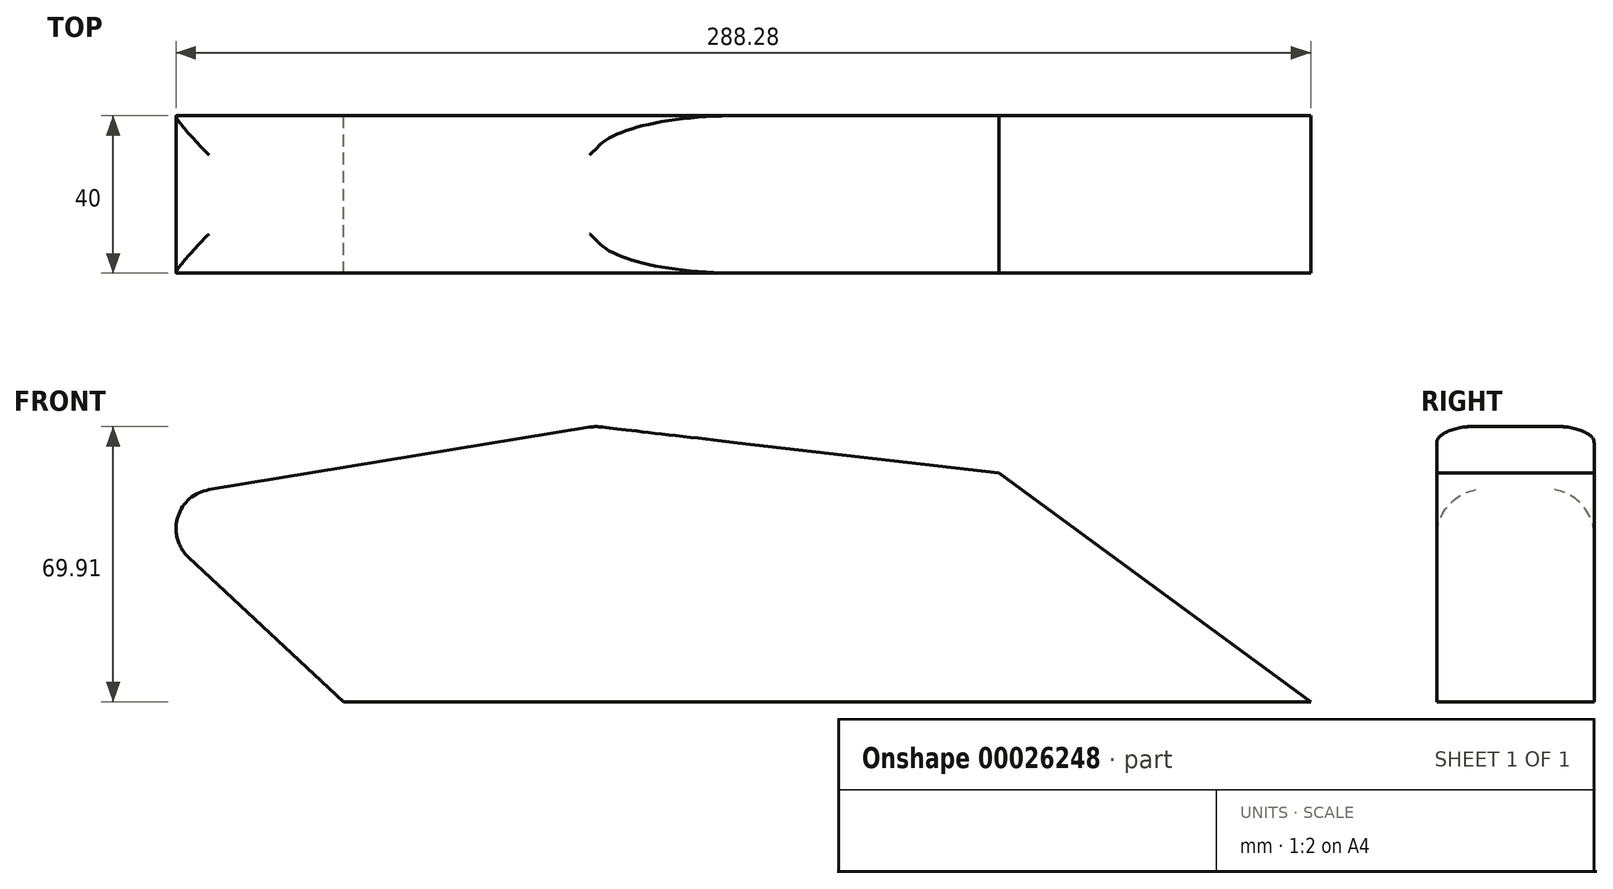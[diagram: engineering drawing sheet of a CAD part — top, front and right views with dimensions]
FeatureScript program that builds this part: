
annotation { "Feature Type Name" : "Feature", "Feature Type Description" : "" }
export const myFeature = defineFeature(function(context is Context, id is Id, definition is map)
    precondition{}
    {
        {
            var Q0;
            Q0=qCreatedBy(makeId("Front.planeOp"),FACE);
            var sketch = newSketch(context, id + "F0", { "sketchPlane" : qUnion([Q0])});
            skLineSegment(sketch, "E0.bottom", {"start": v(-84.2, -32.3) * mm, "end": v(215.8, -32.3) * mm});
            skLineSegment(sketch, "E1", {"start": v(215.8, -32.3) * mm, "end": v(136.6, 25.8) * mm});
            skLineSegment(sketch, "E2", {"start": v(136.6, 25.8) * mm, "end": v(34, 37.7) * mm});
            skLineSegment(sketch, "E3", {"start": v(34, 37.7) * mm, "end": v(-84.2, 18.3) * mm});
            skLineSegment(sketch, "E4", {"start": v(-84.2, 18.3) * mm, "end": v(-29.9, -32.3) * mm});
            skSolve(sketch);
        }
        {
            var Q0;
            Q0=makeQuery(id+"F0.imprint","IMPRINT",FACE,{"disambiguationData":[TD([[makeQuery(id+"F0.imprint","IMPRINT",EDGE,{"derivedFrom":sQuery(id+"F0.wireOp",EDGE,"E0.bottom")}),1.0]])]});
            extrude(context, id + "F1", {"entities" : qUnion([Q0]), "depth" : 40 * mm});
        }
        {
            var Q0;
            Q0=makeQuery(id+"F1.opExtrude","SWEPT_FACE",FACE,{"disambiguationData":[OSD([sQuery(id+"F0.wireOp",EDGE,"E3")])]});
            fillet(context, id + "F2", {"entities" : qUnion([Q0]), "radius" : 10 * mm, "tangentPropagation" : true, "allowEdgeOverflow" : false});
        }
    });
